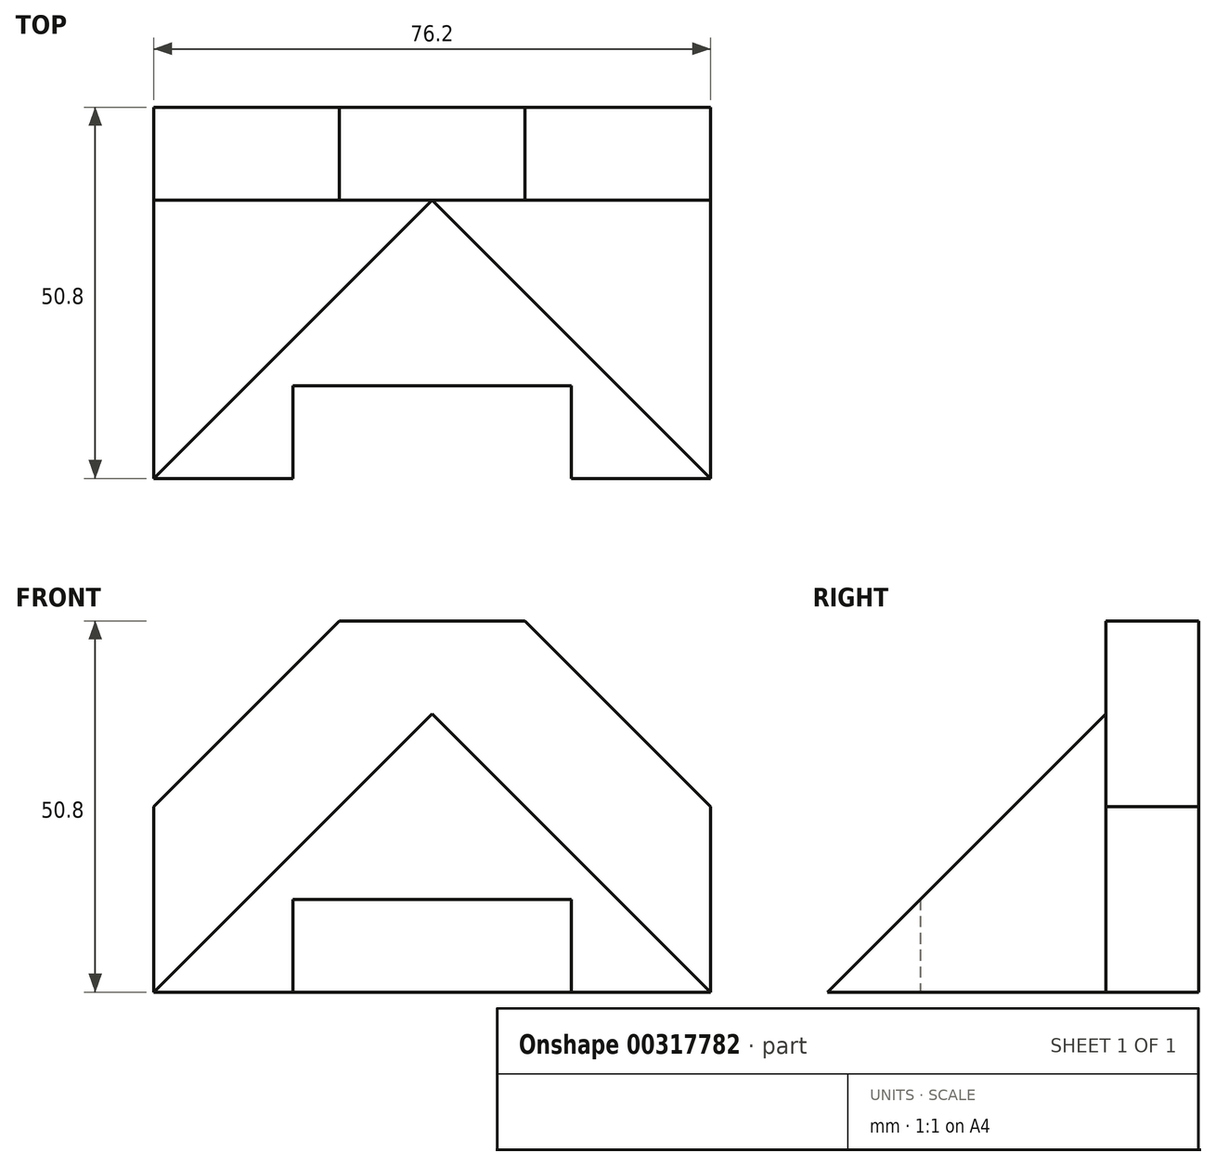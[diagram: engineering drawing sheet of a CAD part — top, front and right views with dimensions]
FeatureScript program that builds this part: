
annotation { "Feature Type Name" : "Feature", "Feature Type Description" : "" }
export const myFeature = defineFeature(function(context is Context, id is Id, definition is map)
    precondition{}
    {
        {
            var Q0;
            Q0=qCreatedBy(makeId("Right.planeOp"),FACE);
            var sketch = newSketch(context, id + "F0", { "sketchPlane" : qUnion([Q0])});
            skLineSegment(sketch, "E0", {"start": v(0, 0) * mm, "end": v(38.1, 0) * mm});
            skLineSegment(sketch, "E1", {"start": v(38.1, 0) * mm, "end": v(38.1, 38.1) * mm});
            skLineSegment(sketch, "E2", {"start": v(38.1, 38.1) * mm, "end": v(0, 0) * mm});
            skLineSegment(sketch, "E3", {"start": v(38.1, 0) * mm, "end": v(50.8, 0) * mm});
            skLineSegment(sketch, "E4", {"start": v(50.8, 0) * mm, "end": v(50.8, 50.8) * mm});
            skLineSegment(sketch, "E5", {"start": v(50.8, 50.8) * mm, "end": v(38.1, 50.8) * mm});
            skLineSegment(sketch, "E6", {"start": v(38.1, 50.8) * mm, "end": v(38.1, 38.1) * mm});
            skSolve(sketch);
        }
        {
            var Q0;
            Q0=makeQuery(id+"F0.imprint","IMPRINT",FACE,{"disambiguationData":[TD([[makeQuery(id+"F0.imprint","IMPRINT",EDGE,{"derivedFrom":sQuery(id+"F0.wireOp",EDGE,"E0")}),1.0]])]});
            var Q1;
            Q1=makeQuery(id+"F0.imprint","IMPRINT",FACE,{"disambiguationData":[TD([[makeQuery(id+"F0.imprint","IMPRINT",EDGE,{"derivedFrom":sQuery(id+"F0.wireOp",EDGE,"E1")}),-1.0]])]});
            extrude(context, id + "F1", {"entities" : qUnion([Q0, Q1]), "depth" : 76.2 * mm});
        }
        {
            var Q0;
            Q0=qCreatedBy(makeId("Front.planeOp"),FACE);
            var sketch = newSketch(context, id + "F2", { "sketchPlane" : qUnion([Q0])});
            skLineSegment(sketch, "E7", {"start": v(0, 0) * mm, "end": v(0, 38.1) * mm});
            skLineSegment(sketch, "E8", {"start": v(0, 38.1) * mm, "end": v(38.1, 38.1) * mm});
            skLineSegment(sketch, "E9", {"start": v(38.1, 38.1) * mm, "end": v(0, 0) * mm});
            skLineSegment(sketch, "E10", {"start": v(38.1, 38.1) * mm, "end": v(76.2, 38.1) * mm});
            skLineSegment(sketch, "E11", {"start": v(76.2, 38.1) * mm, "end": v(76.2, 0) * mm});
            skLineSegment(sketch, "E12", {"start": v(76.2, 0) * mm, "end": v(38.1, 38.1) * mm});
            skSolve(sketch);
        }
        {
            var Q0;
            Q0=makeQuery(id+"F2.imprint","IMPRINT",FACE,{"disambiguationData":[TD([[makeQuery(id+"F2.imprint","IMPRINT",EDGE,{"derivedFrom":sQuery(id+"F2.wireOp",EDGE,"E10")}),-1.0]])]});
            var Q1;
            Q1=makeQuery(id+"F2.imprint","IMPRINT",FACE,{"disambiguationData":[TD([[makeQuery(id+"F2.imprint","IMPRINT",EDGE,{"derivedFrom":sQuery(id+"F2.wireOp",EDGE,"E7")}),-1.0]])]});
            var Q2;
            Q2=makeQuery(id+"F1.opExtrude","SWEPT_FACE",FACE,{"disambiguationData":[OSD([sQuery(id+"F0.wireOp",EDGE,"E6")])]});
            extrude(context, id + "F3", {"entities" : qUnion([Q0, Q1]), "operationType" : NewBodyOperationType.REMOVE, "endBound" : BoundingType.UP_TO_SURFACE, "oppositeDirection" : true, "endBoundEntityFace" : qUnion([Q2]), "depth" : 25.4 * mm});
        }
        {
            var Q0;
            {var subQ0=sQuery(id+"F0.wireOp",EDGE,"E6");Q0=makeQuery(id+"F3.boolean.opBoolean","MERGE",FACE,{"derivedFrom":[makeQuery(id+"F1.opExtrude","SWEPT_FACE",FACE,{"disambiguationData":[OSD([subQ0])]}),makeQuery(id+"F3.opExtrude","CAP_FACE",FACE,{"disambiguationData":[OSD([subQ0]),ownerDisambiguation([makeQuery(id+"F3.opExtrude","SWEPT_BODY",BODY,{"disambiguationData":[OSD([sQuery(id+"F2.wireOp",EDGE,"E7"),sQuery(id+"F2.wireOp",EDGE,"E8"),sQuery(id+"F2.wireOp",EDGE,"E9")])]})])],"isStart":false}),makeQuery(id+"F3.opExtrude","CAP_FACE",FACE,{"disambiguationData":[OSD([subQ0]),ownerDisambiguation([makeQuery(id+"F3.opExtrude","SWEPT_BODY",BODY,{"disambiguationData":[OSD([sQuery(id+"F2.wireOp",EDGE,"E10"),sQuery(id+"F2.wireOp",EDGE,"E11"),sQuery(id+"F2.wireOp",EDGE,"E12")])]})])],"isStart":false})]});}
            var sketch = newSketch(context, id + "F4", { "sketchPlane" : qUnion([Q0])});
            skLineSegment(sketch, "E13", {"start": v(0, 50.8) * mm, "end": v(25.4, 50.8) * mm});
            skLineSegment(sketch, "E14", {"start": v(0, 50.8) * mm, "end": v(0, 25.4) * mm});
            skLineSegment(sketch, "E15", {"start": v(0, 25.4) * mm, "end": v(25.4, 50.8) * mm});
            skLineSegment(sketch, "E16", {"start": v(76.2, 50.8) * mm, "end": v(76.2, 25.4) * mm});
            skLineSegment(sketch, "E17", {"start": v(76.2, 50.8) * mm, "end": v(50.8, 50.8) * mm});
            skLineSegment(sketch, "E18", {"start": v(50.8, 50.8) * mm, "end": v(76.2, 25.4) * mm});
            skSolve(sketch);
        }
        {
            var Q0;
            Q0=makeQuery(id+"F4.imprint","IMPRINT",FACE,{"disambiguationData":[TD([[makeQuery(id+"F4.imprint","IMPRINT",EDGE,{"derivedFrom":sQuery(id+"F4.wireOp",EDGE,"E13")}),1.0]])]});
            var Q1;
            Q1=makeQuery(id+"F4.imprint","IMPRINT",FACE,{"disambiguationData":[TD([[makeQuery(id+"F4.imprint","IMPRINT",EDGE,{"derivedFrom":sQuery(id+"F4.wireOp",EDGE,"E16")}),-1.0]])]});
            extrude(context, id + "F5", {"entities" : qUnion([Q0, Q1]), "operationType" : NewBodyOperationType.REMOVE, "endBound" : BoundingType.THROUGH_ALL, "oppositeDirection" : true, "depth" : 25.4 * mm});
        }
        {
            var Q0;
            Q0=qCreatedBy(makeId("Front.planeOp"),FACE);
            var sketch = newSketch(context, id + "F6", { "sketchPlane" : qUnion([Q0])});
            skLineSegment(sketch, "E19", {"start": v(19.05, 0) * mm, "end": v(57.15, 0) * mm});
            skLineSegment(sketch, "E20", {"start": v(57.15, 0) * mm, "end": v(57.15, 12.7) * mm});
            skLineSegment(sketch, "E21", {"start": v(57.15, 12.7) * mm, "end": v(19.05, 12.7) * mm});
            skLineSegment(sketch, "E22", {"start": v(19.05, 12.7) * mm, "end": v(19.05, 0) * mm});
            skSolve(sketch);
        }
        {
            var Q0;
            Q0=makeQuery(id+"F6.imprint","IMPRINT",FACE,{"disambiguationData":[TD([[makeQuery(id+"F6.imprint","IMPRINT",EDGE,{"derivedFrom":sQuery(id+"F6.wireOp",EDGE,"E19")}),1.0]])]});
            extrude(context, id + "F7", {"entities" : qUnion([Q0]), "operationType" : NewBodyOperationType.REMOVE, "oppositeDirection" : true, "depth" : 12.7 * mm});
        }
    });
